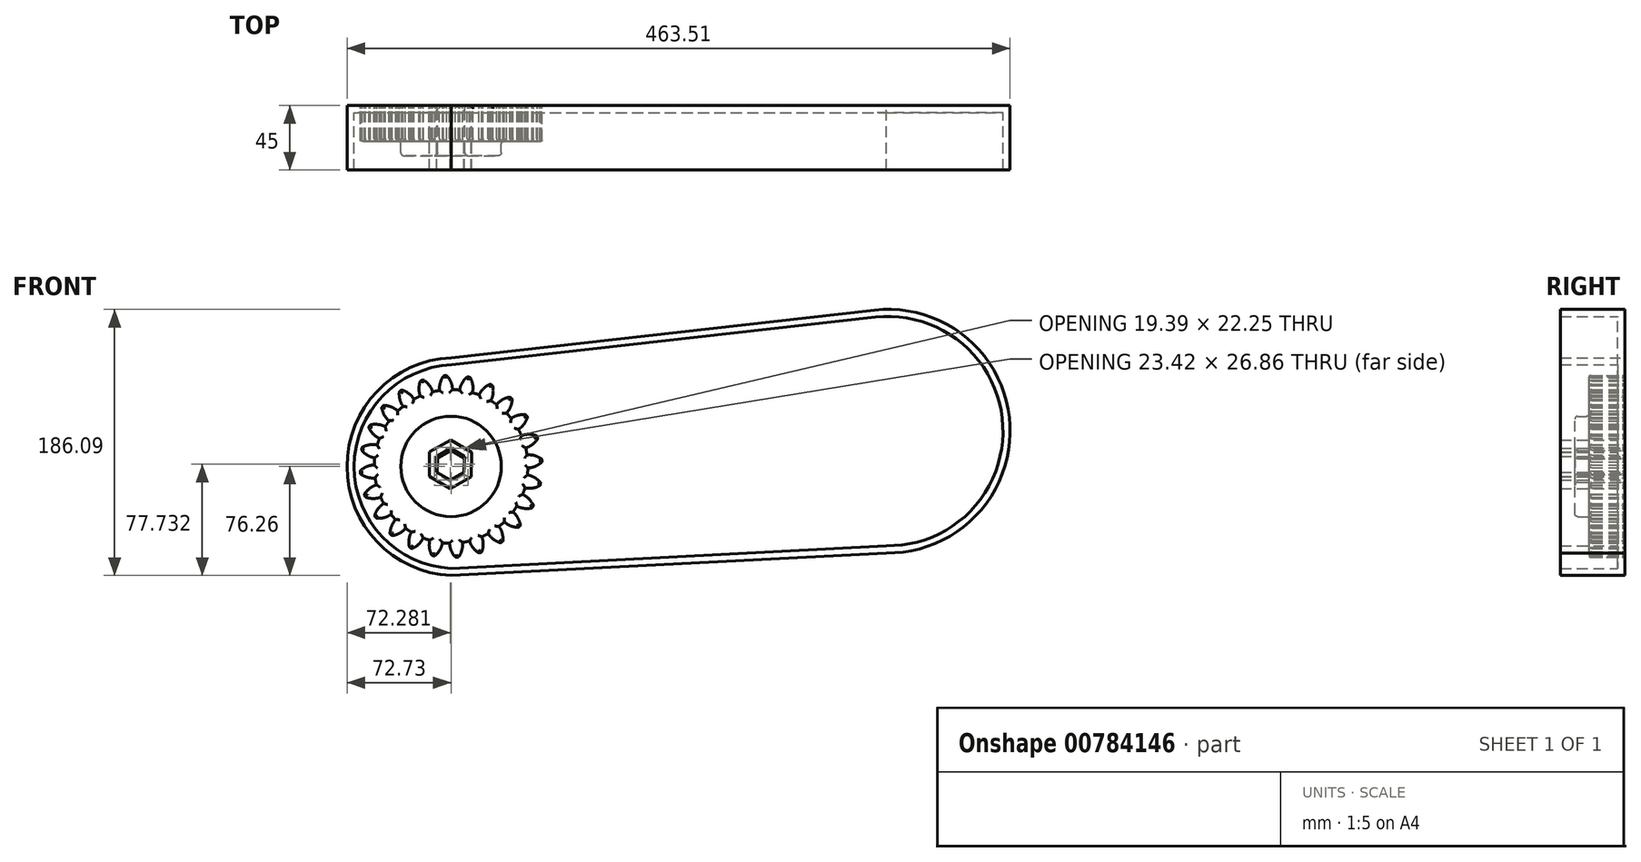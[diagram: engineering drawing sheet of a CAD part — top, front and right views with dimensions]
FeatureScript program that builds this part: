
annotation { "Feature Type Name" : "Feature", "Feature Type Description" : "" }
export const myFeature = defineFeature(function(context is Context, id is Id, definition is map)
    precondition{}
    {
        {
            var Q0;
            Q0=qCreatedBy(makeId("Front.planeOp"),FACE);
            var sketch = newSketch(context, id + "F0", { "sketchPlane" : qUnion([Q0])});
            skCircle(sketch, "E0", {"center": v(0, 0) * mm, "radius": 53.72 * mm});
            skCircle(sketch, "E1", {"center": v(0, 0) * mm, "radius": 58.67 * mm, "construction": true});
            skCircle(sketch, "E2", {"center": v(0, 0) * mm, "radius": 63.5 * mm, "construction": true});
            skLineSegment(sketch, "E3", {"start": v(0, 0) * mm, "end": v(0, 118.64) * mm});
            skLineSegment(sketch, "E4", {"start": v(0, 0) * mm, "end": v(-8.6, 131.21) * mm, "construction": true});
            skLineSegment(sketch, "E5", {"start": v(0, 58.67) * mm, "end": v(-49.7, 57.15) * mm, "construction": true});
            skLineSegment(sketch, "E6", {"start": v(0, 58.67) * mm, "end": v(-55.04, 36.71) * mm, "construction": true});
            skCircle(sketch, "E7", {"center": v(0, 0) * mm, "radius": 54.5 * mm, "construction": true});
            skCircle(sketch, "E8", {"center": v(0, 58.67) * mm, "radius": 14.6 * mm, "construction": true});
            skCircle(sketch, "E9", {"center": v(-13.57, 53.26) * mm, "radius": 14.6 * mm, "construction": true});
            skArc(sketch, "E10", {"start": v(0, 58.67) * mm, "mid": v(-1.31, 61.2) * mm, "end": v(-3.08, 63.43) * mm});
            skArc(sketch, "E11", {"start": v(1.03, 53.71) * mm, "mid": v(0.74, 56.24) * mm, "end": v(0, 58.67) * mm});
            skArc(sketch, "E12.MirrorCS", {"start": v(-7.66, 58.17) * mm, "mid": v(-6.68, 60.84) * mm, "end": v(-5.23, 63.28) * mm});
            skArc(sketch, "E13.MirrorCS", {"start": v(-8.03, 53.12) * mm, "mid": v(-8.08, 55.66) * mm, "end": v(-7.66, 58.17) * mm});
            skArc(sketch, "E14", {"start": v(-3.08, 63.43) * mm, "mid": v(-4.16, 63.5) * mm, "end": v(-5.23, 63.28) * mm});
            skCircle(sketch, "E15", {"center": v(0, 0) * mm, "radius": 35.1 * mm});
            skCircle(sketch, "E16.cCircle", {"center": v(0, 0) * mm, "radius": 9.63 * mm, "construction": true});
            skLineSegment(sketch, "E16.0", {"start": v(9.57, -5.67) * mm, "end": v(-0.13, -11.12) * mm});
            skLineSegment(sketch, "E16.1", {"start": v(-0.13, -11.12) * mm, "end": v(-9.7, -5.45) * mm});
            skLineSegment(sketch, "E16.2", {"start": v(-9.7, -5.45) * mm, "end": v(-9.57, 5.67) * mm});
            skLineSegment(sketch, "E16.3", {"start": v(-9.57, 5.67) * mm, "end": v(0.13, 11.12) * mm});
            skLineSegment(sketch, "E16.4", {"start": v(0.13, 11.12) * mm, "end": v(9.7, 5.45) * mm});
            skLineSegment(sketch, "E16.5", {"start": v(9.7, 5.45) * mm, "end": v(9.57, -5.67) * mm});
            skPoint(sketch, "E16.0.midPoint", {"position": v(4.72, -8.4) * mm});
            skSolve(sketch);
        }
        {
            var Q0;
            Q0=qSketchRegion(id+"F0",true);
            extrude(context, id + "F1", {"entities" : qUnion([Q0]), "depth" : 25 * mm, "offsetDistance" : 25 * mm});
        }
        {
            var Q0;
            Q0=makeQuery(id+"F1.opExtrude","SWEPT_BODY",BODY,{"disambiguationData":[OSD([sQuery(id+"F0.wireOp",EDGE,"E0"),sQuery(id+"F0.wireOp",EDGE,"E10"),sQuery(id+"F0.wireOp",EDGE,"E11"),sQuery(id+"F0.wireOp",EDGE,"E12.MirrorCS"),sQuery(id+"F0.wireOp",EDGE,"E13.MirrorCS"),sQuery(id+"F0.wireOp",EDGE,"E14")])]});
            var Q1;
            Q1=makeQuery(id+"F1.opExtrude","SWEPT_FACE",FACE,{"disambiguationData":[OSD([sQuery(id+"F0.wireOp",EDGE,"E0")])]});
            circularPattern(context, id + "F2", {"entities" : qUnion([Q0]), "axis" : qUnion([Q1]), "angle" : 360 * degree, "instanceCount" : 24, "equalSpace" : true});
        }
        {
            var Q0;
            Q0=makeQuery(id+"F0.imprint","IMPRINT",FACE,{"disambiguationData":[TD([[makeQuery(id+"F0.imprint","IMPRINT",EDGE,{"derivedFrom":sQuery(id+"F0.wireOp",EDGE,"E15")}),1.0]])]});
            extrude(context, id + "F3", {"entities" : qUnion([Q0]), "operationType" : NewBodyOperationType.ADD, "depth" : 35 * mm, "offsetDistance" : 25 * mm});
        }
        {
            var Q0;
            {var subQ0=makeQuery(id+"F1.opExtrude","CAP_FACE",FACE,{"disambiguationData":[OSD([sQuery(id+"F0.wireOp",EDGE,"E0"),sQuery(id+"F0.wireOp",EDGE,"E10"),sQuery(id+"F0.wireOp",EDGE,"E11"),sQuery(id+"F0.wireOp",EDGE,"E12.MirrorCS"),sQuery(id+"F0.wireOp",EDGE,"E13.MirrorCS"),sQuery(id+"F0.wireOp",EDGE,"E14"),sQuery(id+"F0.wireOp",EDGE,"E15")])],"isStart":false});Q0=makeQuery(id+"F3.boolean.opBoolean","MERGE",FACE,{"derivedFrom":[subQ0,makeQuery(id+"F2.opPattern","COPY",FACE,{"derivedFrom":subQ0,"instanceName":"1"}),makeQuery(id+"F2.opPattern","COPY",FACE,{"derivedFrom":subQ0,"instanceName":"2"}),makeQuery(id+"F2.opPattern","COPY",FACE,{"derivedFrom":subQ0,"instanceName":"3"}),makeQuery(id+"F2.opPattern","COPY",FACE,{"derivedFrom":subQ0,"instanceName":"4"}),makeQuery(id+"F2.opPattern","COPY",FACE,{"derivedFrom":subQ0,"instanceName":"5"}),makeQuery(id+"F2.opPattern","COPY",FACE,{"derivedFrom":subQ0,"instanceName":"6"}),makeQuery(id+"F2.opPattern","COPY",FACE,{"derivedFrom":subQ0,"instanceName":"7"}),makeQuery(id+"F2.opPattern","COPY",FACE,{"derivedFrom":subQ0,"instanceName":"8"}),makeQuery(id+"F2.opPattern","COPY",FACE,{"derivedFrom":subQ0,"instanceName":"9"}),makeQuery(id+"F2.opPattern","COPY",FACE,{"derivedFrom":subQ0,"instanceName":"10"}),makeQuery(id+"F2.opPattern","COPY",FACE,{"derivedFrom":subQ0,"instanceName":"11"}),makeQuery(id+"F2.opPattern","COPY",FACE,{"derivedFrom":subQ0,"instanceName":"12"}),makeQuery(id+"F2.opPattern","COPY",FACE,{"derivedFrom":subQ0,"instanceName":"13"}),makeQuery(id+"F2.opPattern","COPY",FACE,{"derivedFrom":subQ0,"instanceName":"14"}),makeQuery(id+"F2.opPattern","COPY",FACE,{"derivedFrom":subQ0,"instanceName":"15"}),makeQuery(id+"F2.opPattern","COPY",FACE,{"derivedFrom":subQ0,"instanceName":"16"}),makeQuery(id+"F2.opPattern","COPY",FACE,{"derivedFrom":subQ0,"instanceName":"17"}),makeQuery(id+"F2.opPattern","COPY",FACE,{"derivedFrom":subQ0,"instanceName":"18"}),makeQuery(id+"F2.opPattern","COPY",FACE,{"derivedFrom":subQ0,"instanceName":"19"}),makeQuery(id+"F2.opPattern","COPY",FACE,{"derivedFrom":subQ0,"instanceName":"20"}),makeQuery(id+"F2.opPattern","COPY",FACE,{"derivedFrom":subQ0,"instanceName":"21"}),makeQuery(id+"F2.opPattern","COPY",FACE,{"derivedFrom":subQ0,"instanceName":"22"}),makeQuery(id+"F2.opPattern","COPY",FACE,{"derivedFrom":subQ0,"instanceName":"23"})]});}
            var Q1;
            Q1=makeQuery(id+"F3.opExtrude","CAP_FACE",FACE,{"disambiguationData":[OSD([sQuery(id+"F0.wireOp",EDGE,"E15"),sQuery(id+"F0.wireOp",EDGE,"E16.0"),sQuery(id+"F0.wireOp",EDGE,"E16.1"),sQuery(id+"F0.wireOp",EDGE,"E16.2"),sQuery(id+"F0.wireOp",EDGE,"E16.3"),sQuery(id+"F0.wireOp",EDGE,"E16.4"),sQuery(id+"F0.wireOp",EDGE,"E16.5")])],"isStart":false});
            var Q2;
            {var subQ0=sQuery(id+"F0.wireOp",EDGE,"E15");var subQ1=makeQuery(id+"F1.opExtrude","CAP_FACE",FACE,{"disambiguationData":[OSD([sQuery(id+"F0.wireOp",EDGE,"E0"),sQuery(id+"F0.wireOp",EDGE,"E10"),sQuery(id+"F0.wireOp",EDGE,"E11"),sQuery(id+"F0.wireOp",EDGE,"E12.MirrorCS"),sQuery(id+"F0.wireOp",EDGE,"E13.MirrorCS"),sQuery(id+"F0.wireOp",EDGE,"E14"),subQ0])],"isStart":true});Q2=makeQuery(id+"F3.boolean.opBoolean","MERGE",FACE,{"derivedFrom":[subQ1,makeQuery(id+"F2.opPattern","COPY",FACE,{"derivedFrom":subQ1,"instanceName":"1"}),makeQuery(id+"F2.opPattern","COPY",FACE,{"derivedFrom":subQ1,"instanceName":"2"}),makeQuery(id+"F2.opPattern","COPY",FACE,{"derivedFrom":subQ1,"instanceName":"3"}),makeQuery(id+"F2.opPattern","COPY",FACE,{"derivedFrom":subQ1,"instanceName":"4"}),makeQuery(id+"F2.opPattern","COPY",FACE,{"derivedFrom":subQ1,"instanceName":"5"}),makeQuery(id+"F2.opPattern","COPY",FACE,{"derivedFrom":subQ1,"instanceName":"6"}),makeQuery(id+"F2.opPattern","COPY",FACE,{"derivedFrom":subQ1,"instanceName":"7"}),makeQuery(id+"F2.opPattern","COPY",FACE,{"derivedFrom":subQ1,"instanceName":"8"}),makeQuery(id+"F2.opPattern","COPY",FACE,{"derivedFrom":subQ1,"instanceName":"9"}),makeQuery(id+"F2.opPattern","COPY",FACE,{"derivedFrom":subQ1,"instanceName":"10"}),makeQuery(id+"F2.opPattern","COPY",FACE,{"derivedFrom":subQ1,"instanceName":"11"}),makeQuery(id+"F2.opPattern","COPY",FACE,{"derivedFrom":subQ1,"instanceName":"12"}),makeQuery(id+"F2.opPattern","COPY",FACE,{"derivedFrom":subQ1,"instanceName":"13"}),makeQuery(id+"F2.opPattern","COPY",FACE,{"derivedFrom":subQ1,"instanceName":"14"}),makeQuery(id+"F2.opPattern","COPY",FACE,{"derivedFrom":subQ1,"instanceName":"15"}),makeQuery(id+"F2.opPattern","COPY",FACE,{"derivedFrom":subQ1,"instanceName":"16"}),makeQuery(id+"F2.opPattern","COPY",FACE,{"derivedFrom":subQ1,"instanceName":"17"}),makeQuery(id+"F2.opPattern","COPY",FACE,{"derivedFrom":subQ1,"instanceName":"18"}),makeQuery(id+"F2.opPattern","COPY",FACE,{"derivedFrom":subQ1,"instanceName":"19"}),makeQuery(id+"F2.opPattern","COPY",FACE,{"derivedFrom":subQ1,"instanceName":"20"}),makeQuery(id+"F2.opPattern","COPY",FACE,{"derivedFrom":subQ1,"instanceName":"21"}),makeQuery(id+"F2.opPattern","COPY",FACE,{"derivedFrom":subQ1,"instanceName":"22"}),makeQuery(id+"F2.opPattern","COPY",FACE,{"derivedFrom":subQ1,"instanceName":"23"}),makeQuery(id+"F3.opExtrude","CAP_FACE",FACE,{"disambiguationData":[OSD([subQ0,sQuery(id+"F0.wireOp",EDGE,"E16.0"),sQuery(id+"F0.wireOp",EDGE,"E16.1"),sQuery(id+"F0.wireOp",EDGE,"E16.2"),sQuery(id+"F0.wireOp",EDGE,"E16.3"),sQuery(id+"F0.wireOp",EDGE,"E16.4"),sQuery(id+"F0.wireOp",EDGE,"E16.5")])],"isStart":true})]});}
            fillet(context, id + "F4", {"entities" : qUnion([Q0, Q1, Q2]), "radius" : 2 * mm, "tangentPropagation" : true, "allowEdgeOverflow" : false});
        }
        {
            var Q0;
            Q0=qCreatedBy(makeId("Front.planeOp"),FACE);
            var sketch = newSketch(context, id + "F5", { "sketchPlane" : qUnion([Q0])});
            skArc(sketch, "E17", {"start": v(0, 76.03) * mm, "mid": v(-72.73, -0.11) * mm, "end": v(0, -76.26) * mm});
            skLineSegment(sketch, "E18", {"start": v(0, 76.03) * mm, "end": v(296.13, 109.3) * mm});
            skArc(sketch, "E19", {"start": v(304.25, -60.46) * mm, "mid": v(390.69, 28.74) * mm, "end": v(296.13, 109.3) * mm});
            skLineSegment(sketch, "E20", {"start": v(0, -76.26) * mm, "end": v(304.25, -60.46) * mm});
            skLineSegment(sketch, "E21.0", {"start": v(9.12, -4.2) * mm, "end": v(-0.57, -9.65) * mm});
            skLineSegment(sketch, "E21.1", {"start": v(-0.57, -9.65) * mm, "end": v(-10.14, -3.98) * mm});
            skLineSegment(sketch, "E21.2", {"start": v(-10.14, -3.98) * mm, "end": v(-10.02, 7.14) * mm});
            skLineSegment(sketch, "E21.3", {"start": v(-10.02, 7.14) * mm, "end": v(-0.32, 12.6) * mm});
            skLineSegment(sketch, "E21.4", {"start": v(-0.32, 12.6) * mm, "end": v(9.25, 6.92) * mm});
            skLineSegment(sketch, "E21.5", {"start": v(9.25, 6.92) * mm, "end": v(9.12, -4.2) * mm});
            skSolve(sketch);
        }
        {
            var Q0;
            Q0=makeQuery(id+"F5.imprint","IMPRINT",FACE,{"disambiguationData":[TD([[makeQuery(id+"F5.imprint","IMPRINT",EDGE,{"derivedFrom":sQuery(id+"F5.wireOp",EDGE,"E17")}),1.0]])]});
            extrude(context, id + "F6", {"entities" : qUnion([Q0]), "depth" : 45 * mm, "offsetDistance" : 25 * mm});
        }
        {
            var Q0;
            Q0=makeQuery(id+"F6.opExtrude","CAP_FACE",FACE,{"disambiguationData":[OSD([sQuery(id+"F5.wireOp",EDGE,"E17"),sQuery(id+"F5.wireOp",EDGE,"E18"),sQuery(id+"F5.wireOp",EDGE,"E19"),sQuery(id+"F5.wireOp",EDGE,"E20")])],"isStart":false});
            var Q1;
            Q1=makeQuery(id+"F6.opExtrude","SWEPT_BODY",BODY,{"disambiguationData":[OSD([sQuery(id+"F5.wireOp",EDGE,"E17"),sQuery(id+"F5.wireOp",EDGE,"E18"),sQuery(id+"F5.wireOp",EDGE,"E19"),sQuery(id+"F5.wireOp",EDGE,"E20")])]});
            shell(context, id + "F7", {"entities" : qUnion([Q0]), "parts" : qUnion([Q1]), "thickness" : 5 * mm});
        }
    });
